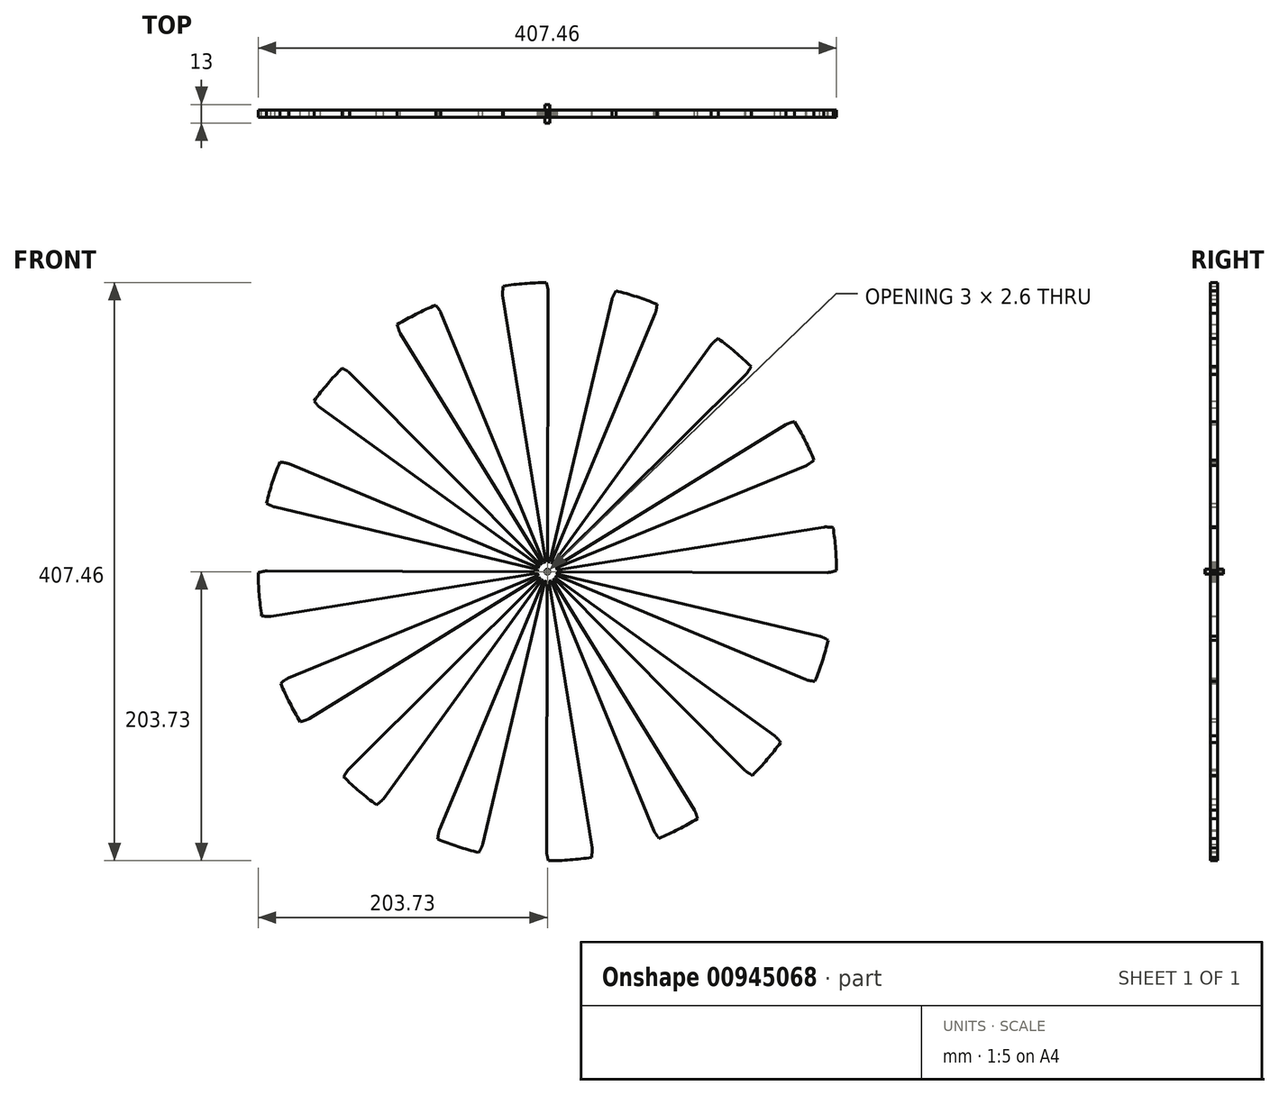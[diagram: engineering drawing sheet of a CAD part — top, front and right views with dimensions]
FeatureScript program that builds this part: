
annotation { "Feature Type Name" : "Feature", "Feature Type Description" : "" }
export const myFeature = defineFeature(function(context is Context, id is Id, definition is map)
    precondition{}
    {
        {
            assignVariable(context, id + "F0", {"name" : "Teeth", "anyValue" : 16});
        }
        {
            var Q0;
            Q0=qCreatedBy(makeId("Front.planeOp"),FACE);
            var sketch = newSketch(context, id + "F1", { "sketchPlane" : qUnion([Q0])});
            skCircle(sketch, "E0", {"center": v(0, 0) * mm, "radius": 7.73 * mm, "construction": true});
            skLineSegment(sketch, "E1", {"start": v(0, 0) * mm, "end": v(-0.42, 7.72) * mm, "construction": true});
            skLineSegment(sketch, "E2", {"start": v(0, 0) * mm, "end": v(-0.88, 7.68) * mm, "construction": true});
            skLineSegment(sketch, "E3", {"start": v(0, 0) * mm, "end": v(-1.35, 7.6) * mm, "construction": true});
            skLineSegment(sketch, "E4", {"start": v(-1.35, 7.6) * mm, "end": v(0.03, 7.85) * mm, "construction": true});
            skLineSegment(sketch, "E5", {"start": v(0, 0) * mm, "end": v(-1.8, 7.51) * mm, "construction": true});
            skLineSegment(sketch, "E6", {"start": v(-1.8, 7.51) * mm, "end": v(0.01, 7.95) * mm, "construction": true});
            skLineSegment(sketch, "E7", {"start": v(-1.35, 7.6) * mm, "end": v(-0.88, 7.68) * mm, "construction": true});
            skLineSegment(sketch, "E8", {"start": v(-1.8, 7.51) * mm, "end": v(-1.35, 7.6) * mm, "construction": true});
            skLineSegment(sketch, "E9", {"start": v(-1.35, 7.6) * mm, "end": v(-0.42, 7.72) * mm, "construction": true});
            skLineSegment(sketch, "E10", {"start": v(-1.8, 7.51) * mm, "end": v(-0.42, 7.72) * mm, "construction": true});
            skLineSegment(sketch, "E11", {"start": v(0, 0) * mm, "end": v(-3.14, 7.06) * mm, "construction": true});
            skLineSegment(sketch, "E12", {"start": v(-3.14, 7.06) * mm, "end": v(-0.16, 8.38) * mm, "construction": true});
            skLineSegment(sketch, "E13", {"start": v(0, 0) * mm, "end": v(-2.7, 7.24) * mm, "construction": true});
            skLineSegment(sketch, "E14", {"start": v(-2.7, 7.24) * mm, "end": v(-0.08, 8.22) * mm, "construction": true});
            skLineSegment(sketch, "E15", {"start": v(0, 0) * mm, "end": v(-2.26, 7.4) * mm, "construction": true});
            skLineSegment(sketch, "E16", {"start": v(-2.26, 7.4) * mm, "end": v(-0.03, 8.07) * mm, "construction": true});
            skLineSegment(sketch, "E17", {"start": v(-2.26, 7.4) * mm, "end": v(-1.8, 7.51) * mm, "construction": true});
            skLineSegment(sketch, "E18", {"start": v(-2.26, 7.4) * mm, "end": v(-2.7, 7.24) * mm, "construction": true});
            skLineSegment(sketch, "E19", {"start": v(-2.7, 7.24) * mm, "end": v(-3.14, 7.06) * mm, "construction": true});
            skLineSegment(sketch, "E20", {"start": v(-2.26, 7.4) * mm, "end": v(-0.42, 7.72) * mm, "construction": true});
            skLineSegment(sketch, "E21", {"start": v(-2.7, 7.24) * mm, "end": v(-0.42, 7.72) * mm, "construction": true});
            skLineSegment(sketch, "E22", {"start": v(-3.14, 7.06) * mm, "end": v(-0.42, 7.72) * mm, "construction": true});
            skLineSegment(sketch, "E23", {"start": v(0, 0) * mm, "end": v(-3.97, 6.63) * mm, "construction": true});
            skLineSegment(sketch, "E24", {"start": v(-3.97, 6.63) * mm, "end": v(-0.4, 8.77) * mm, "construction": true});
            skLineSegment(sketch, "E25", {"start": v(0, 0) * mm, "end": v(-4.36, 6.38) * mm, "construction": true});
            skLineSegment(sketch, "E26", {"start": v(-4.36, 6.38) * mm, "end": v(-0.55, 8.98) * mm, "construction": true});
            skLineSegment(sketch, "E27", {"start": v(0, 0) * mm, "end": v(-4.74, 6.1) * mm, "construction": true});
            skLineSegment(sketch, "E28", {"start": v(0, 0) * mm, "end": v(-3.56, 6.86) * mm, "construction": true});
            skLineSegment(sketch, "E29", {"start": v(-3.56, 6.86) * mm, "end": v(-0.26, 8.57) * mm, "construction": true});
            skLineSegment(sketch, "E30", {"start": v(-3.14, 7.06) * mm, "end": v(-3.56, 6.86) * mm, "construction": true});
            skLineSegment(sketch, "E31", {"start": v(-3.56, 6.86) * mm, "end": v(-3.97, 6.63) * mm, "construction": true});
            skLineSegment(sketch, "E32", {"start": v(-3.97, 6.63) * mm, "end": v(-4.36, 6.38) * mm, "construction": true});
            skLineSegment(sketch, "E33", {"start": v(-4.36, 6.38) * mm, "end": v(-4.74, 6.1) * mm, "construction": true});
            skLineSegment(sketch, "E34", {"start": v(-0.42, 7.72) * mm, "end": v(-3.56, 6.86) * mm, "construction": true});
            skLineSegment(sketch, "E35", {"start": v(-0.42, 7.72) * mm, "end": v(-3.97, 6.63) * mm, "construction": true});
            skLineSegment(sketch, "E36", {"start": v(-0.42, 7.72) * mm, "end": v(-4.36, 6.38) * mm, "construction": true});
            skLineSegment(sketch, "E37", {"start": v(-0.42, 7.72) * mm, "end": v(-4.74, 6.1) * mm, "construction": true});
            skCircle(sketch, "E38", {"center": v(0, 0) * mm, "radius": 8 * mm, "construction": true});
            skCircle(sketch, "E39", {"center": v(0, 0) * mm, "radius": 9 * mm});
            skPoint(sketch, "E40", {"position": v(0, 8) * mm});
            skLineSegment(sketch, "E41", {"start": v(0, 0) * mm, "end": v(-0.84, 8.56) * mm, "construction": true});
            skPoint(sketch, "E42.MirrorP", {"position": v(-1.56, 7.85) * mm});
            skLineSegment(sketch, "E43", {"start": v(-1.56, 7.85) * mm, "end": v(0, 0) * mm, "construction": true});
            skLineSegment(sketch, "E44", {"start": v(0, 0) * mm, "end": v(0, 8) * mm, "construction": true});
            skLineSegment(sketch, "E45", {"start": v(-0.88, 7.68) * mm, "end": v(-0.42, 7.72) * mm, "construction": true});
            skLineSegment(sketch, "E46", {"start": v(0.03, 7.85) * mm, "end": v(0.01, 7.95) * mm, "construction": true});
            skLineSegment(sketch, "E47", {"start": v(0, 0) * mm, "end": v(0, 10.19) * mm, "construction": true});
            skCircle(sketch, "E48", {"center": v(0, 0) * mm, "radius": 7 * mm});
            skSolve(sketch);
        }
        {
            var Q0;
            Q0=qCreatedBy(makeId("Front.planeOp"),FACE);
            var sketch = newSketch(context, id + "F2", { "sketchPlane" : qUnion([Q0])});
            skCircle(sketch, "E49.0", {"center": v(0, 0) * mm, "radius": 8 * mm, "construction": true});
            skPoint(sketch, "E50.0", {"position": v(-0.55, 8.98) * mm});
            skPoint(sketch, "E50.1", {"position": v(-0.4, 8.77) * mm});
            skPoint(sketch, "E50.2", {"position": v(-0.26, 8.57) * mm});
            skPoint(sketch, "E50.3", {"position": v(-0.16, 8.38) * mm});
            skPoint(sketch, "E50.4", {"position": v(-0.08, 8.22) * mm});
            skPoint(sketch, "E50.6", {"position": v(0.01, 7.95) * mm});
            skPoint(sketch, "E50.7", {"position": v(0.03, 7.85) * mm});
            skPoint(sketch, "E50.8", {"position": v(-0.03, 8.07) * mm});
            skLineSegment(sketch, "E51.0", {"start": v(0, 0) * mm, "end": v(-0.84, 8.56) * mm, "construction": true});
            skFitSpline(sketch, "E52", {"points": [v(-0.77, 203.73) * mm, v(-0.39, 202.42) * mm, v(-0.08, 201.25) * mm, v(0.16, 200.2) * mm, v(0.34, 199.29) * mm, v(0.47, 198.5) * mm, v(0.56, 197.87) * mm, v(0.6, 197.37) * mm], "startDerivative": vector(6.57, -22.38) * mm, "endDerivative": vector(1.47, -14.1) * mm});
            skFitSpline(sketch, "E53.MirrorCS", {"points": [v(-31.11, 201.34) * mm, v(-31.28, 200) * mm, v(-31.4, 198.78) * mm, v(-31.48, 197.7) * mm, v(-31.51, 196.78) * mm, v(-31.52, 196) * mm, v(-31.5, 195.35) * mm, v(-31.48, 194.85) * mm], "startDerivative": vector(-2.99, -23.13) * mm, "endDerivative": vector(0.76, -14.15) * mm});
            skCircle(sketch, "E54", {"center": v(0, 0) * mm, "radius": 0.05 * mm});
            skCircle(sketch, "E55.0", {"center": v(0, 0) * mm, "radius": 7 * mm});
            skArc(sketch, "E56", {"start": v(-0.77, 203.73) * mm, "mid": v(-15.98, 203.1) * mm, "end": v(-31.11, 201.34) * mm});
            skLineSegment(sketch, "E57", {"start": v(-31.48, 194.85) * mm, "end": v(0, 0) * mm});
            skLineSegment(sketch, "E58", {"start": v(0, 0) * mm, "end": v(0.6, 197.37) * mm});
            skSolve(sketch);
        }
        {
            var Q0;
            {var subQ1=sQuery(id+"F2.wireOp",EDGE,"E52");var subQ9=sQuery(id+"F2.wireOp",EDGE,"rA0usyOi-Jm6w-jZNR-JSDv-ujEcH4bsm2Ol");var subQ11=makeQuery(id+"F2.imprint","INTERSECT",VERTEX,{"derivedFrom":[subQ1,subQ9]});Q0=makeQuery(id+"F2.imprint","IMPRINT",FACE,{"disambiguationData":[TD([[makeQuery(id+"F2.imprint","IMPRINT",EDGE,{"disambiguationData":[TD([[subQ11,1.0]])],"derivedFrom":subQ1}),-1.0]])]});}
            var Q1;
            {var subQ0=sQuery(id+"F2.wireOp",EDGE,"QqPcIgQ4-TZE6-73E5-WQaq-ugCT5JtziKyn");var subQ1=sQuery(id+"F2.wireOp",EDGE,"90be38e0-c88f-493d-85a8-1201295b9109.0");var subQ2=makeQuery(id+"F2.imprint","INTERSECT",VERTEX,{"derivedFrom":[subQ1,subQ0]});Q1=makeQuery(id+"F2.imprint","IMPRINT",FACE,{"disambiguationData":[TD([[makeQuery(id+"F2.imprint","IMPRINT",EDGE,{"disambiguationData":[TD([[subQ2,1.0]])],"derivedFrom":subQ1}),1.0]])]});}
            var Q2;
            {var subQ0=sQuery(id+"F2.wireOp",EDGE,"QqPcIgQ4-TZE6-73E5-WQaq-ugCT5JtziKyn");var subQ1=sQuery(id+"F2.wireOp",EDGE,"90be38e0-c88f-493d-85a8-1201295b9109.0");var subQ2=makeQuery(id+"F2.imprint","INTERSECT",VERTEX,{"derivedFrom":[subQ1,subQ0]});Q2=makeQuery(id+"F2.imprint","IMPRINT",FACE,{"disambiguationData":[TD([[makeQuery(id+"F2.imprint","IMPRINT",EDGE,{"disambiguationData":[TD([[subQ2,-1.0]])],"derivedFrom":subQ1}),1.0]])]});}
            var Q3;
            {var subQ1=sQuery(id+"F2.wireOp",EDGE,"E52");var subQ8=sQuery(id+"F2.wireOp",EDGE,"b861a5ab-cd51-40f1-92ab-cea0f5fe0d4d.1");var subQ11=makeQuery(id+"F2.imprint","INTERSECT",VERTEX,{"derivedFrom":[subQ1,subQ8]});Q3=makeQuery(id+"F2.imprint","IMPRINT",FACE,{"disambiguationData":[TD([[makeQuery(id+"F2.imprint","IMPRINT",EDGE,{"disambiguationData":[TD([[subQ11,1.0]])],"derivedFrom":subQ1}),-1.0]])]});}
            var Q4;
            {var subQ0=sQuery(id+"F2.wireOp",EDGE,"b861a5ab-cd51-40f1-92ab-cea0f5fe0d4d.0");var subQ1=sQuery(id+"F2.wireOp",EDGE,"E54");var subQ2=makeQuery(id+"F2.imprint","INTERSECT",VERTEX,{"derivedFrom":[subQ1,subQ0]});Q4=makeQuery(id+"F2.imprint","IMPRINT",FACE,{"disambiguationData":[TD([[makeQuery(id+"F2.imprint","IMPRINT",EDGE,{"disambiguationData":[TD([[subQ2,-1.0]])],"derivedFrom":subQ1}),-1.0]])]});}
            var Q5;
            {var subQ0=sQuery(id+"F2.wireOp",EDGE,"b861a5ab-cd51-40f1-92ab-cea0f5fe0d4d.0");var subQ1=sQuery(id+"F2.wireOp",EDGE,"E54");var subQ2=makeQuery(id+"F2.imprint","INTERSECT",VERTEX,{"derivedFrom":[subQ1,subQ0]});Q5=makeQuery(id+"F2.imprint","IMPRINT",FACE,{"disambiguationData":[TD([[makeQuery(id+"F2.imprint","IMPRINT",EDGE,{"disambiguationData":[TD([[subQ2,1.0]])],"derivedFrom":subQ1}),-1.0]])]});}
            extrude(context, id + "F3", {"entities" : qUnion([Q0, Q1, Q2, Q3, Q4, Q5]), "offsetDistance" : 25 * mm, "depth" : 5 * mm, "symmetric" : true});
        }
        {
            var Q0;
            Q0=makeQuery(id+"FdV6txGXfAbNHnU_2.opFillet","BLEND_FACE",FACE,{"disambiguationData":[OSD([sQuery(id+"F2.wireOp",EDGE,"E55.0"),sQuery(id+"F2.wireOp",EDGE,"E57")])]});
            var Q1;
            Q1=makeQuery(id+"F3.opExtrude","SWEPT_FACE",FACE,{"disambiguationData":[OSD([sQuery(id+"F2.wireOp",EDGE,"E57")])]});
            var Q2;
            Q2=makeQuery(id+"F3.opExtrude","SWEPT_FACE",FACE,{"disambiguationData":[OSD([sQuery(id+"F2.wireOp",EDGE,"E53.MirrorCS")])]});
            var Q3;
            Q3=makeQuery(id+"F3.opExtrude","SWEPT_FACE",FACE,{"disambiguationData":[OSD([sQuery(id+"F2.wireOp",EDGE,"E56")])]});
            var Q4;
            Q4=makeQuery(id+"F3.opExtrude","SWEPT_FACE",FACE,{"disambiguationData":[OSD([sQuery(id+"F2.wireOp",EDGE,"E52")])]});
            var Q5;
            Q5=makeQuery(id+"F3.opExtrude","SWEPT_FACE",FACE,{"disambiguationData":[OSD([sQuery(id+"F2.wireOp",EDGE,"E58")])]});
            var Q6;
            Q6=makeQuery(id+"FdV6txGXfAbNHnU_2.opFillet","BLEND_FACE",FACE,{"disambiguationData":[OSD([sQuery(id+"F2.wireOp",EDGE,"E55.0"),sQuery(id+"F2.wireOp",EDGE,"E58")])]});
            var Q7;
            Q7=makeQuery(id+"F3.opExtrude","SWEPT_FACE",FACE,{"disambiguationData":[OSD([sQuery(id+"F2.wireOp",EDGE,"E55.0")])]});
            circularPattern(context, id + "F4", {"faces" : qUnion([Q0, Q1, Q2, Q3, Q4, Q5, Q6]), "axis" : qUnion([Q7]), "angle" : 360 * degree, "instanceCount" : round(getVariable(context, 'Teeth')), "equalSpace" : true, "patternType" : PatternType.FACE});
        }
        {
            var Q0;
            Q0=qCreatedBy(makeId("Front.planeOp"),FACE);
            var sketch = newSketch(context, id + "F5", { "sketchPlane" : qUnion([Q0])});
            skCircle(sketch, "E59", {"center": v(0, 0) * mm, "radius": 6.5 * mm});
            skSolve(sketch);
        }
        {
            var Q0;
            Q0=makeQuery(id+"F5.imprint","IMPRINT",FACE,{"disambiguationData":[TD([[makeQuery(id+"F5.imprint","IMPRINT",EDGE,{"derivedFrom":sQuery(id+"F5.wireOp",EDGE,"E59")}),1.0]])]});
            extrude(context, id + "F6", {"entities" : qUnion([Q0]), "operationType" : NewBodyOperationType.ADD, "depth" : 2 * mm, "offsetDistance" : 25 * mm, "symmetric" : true});
        }
        {
            var Q0;
            Q0=qCreatedBy(makeId("Front.planeOp"),FACE);
            var sketch = newSketch(context, id + "F7", { "sketchPlane" : qUnion([Q0])});
            skArc(sketch, "E60", {"start": v(-0.5, 2.96) * mm, "mid": v(-1.83, 2.38) * mm, "end": v(-2.73, 1.25) * mm});
            skLineSegment(sketch, "E61", {"start": v(-2.73, 1.25) * mm, "end": v(-5.36, 1.25) * mm});
            skLineSegment(sketch, "E62", {"start": v(-0.5, 2.96) * mm, "end": v(-0.5, 5.48) * mm});
            skLineSegment(sketch, "E63.MirrorCS", {"start": v(-2.73, -1.25) * mm, "end": v(-5.36, -1.25) * mm});
            skLineSegment(sketch, "E64.MirrorCS", {"start": v(0.5, 2.96) * mm, "end": v(0.5, 5.48) * mm});
            skLineSegment(sketch, "E65.MirrorCS", {"start": v(2.73, 1.25) * mm, "end": v(5.36, 1.25) * mm});
            skLineSegment(sketch, "E66.MirrorCS", {"start": v(2.73, -1.25) * mm, "end": v(5.36, -1.25) * mm});
            skLineSegment(sketch, "E67.MirrorCS", {"start": v(-0.5, -2.96) * mm, "end": v(-0.5, -5.48) * mm});
            skLineSegment(sketch, "E68.MirrorCS", {"start": v(0.5, -2.96) * mm, "end": v(0.5, -5.48) * mm});
            skArc(sketch, "E69.trimOffspring", {"start": v(-2.73, -1.25) * mm, "mid": v(-1.83, -2.38) * mm, "end": v(-0.5, -2.96) * mm});
            skArc(sketch, "E70.trimOffspring", {"start": v(0.5, -2.96) * mm, "mid": v(1.83, -2.38) * mm, "end": v(2.73, -1.25) * mm});
            skArc(sketch, "E71.trimOffspring", {"start": v(2.73, 1.25) * mm, "mid": v(1.83, 2.38) * mm, "end": v(0.5, 2.96) * mm});
            skArc(sketch, "E72", {"start": v(0.5, 5.48) * mm, "mid": v(0, 5.5) * mm, "end": v(-0.5, 5.48) * mm});
            skArc(sketch, "E73.trimOffspring", {"start": v(5.36, -1.25) * mm, "mid": v(5.5, 0) * mm, "end": v(5.36, 1.25) * mm});
            skArc(sketch, "E74.trimOffspring", {"start": v(-0.5, -5.48) * mm, "mid": v(0, -5.5) * mm, "end": v(0.5, -5.48) * mm});
            skArc(sketch, "E75.trimOffspring", {"start": v(-5.36, 1.25) * mm, "mid": v(-5.5, 0) * mm, "end": v(-5.36, -1.25) * mm});
            skSolve(sketch);
        }
        {
            var Q0;
            Q0 = qSketchRegion(id + "F7", true);
            extrude(context, id + "F8", {"entities" : qUnion([Q0]), "operationType" : NewBodyOperationType.ADD, "depth" : 4 * mm, "offsetDistance" : 25 * mm, "symmetric" : true});
        }
        {
            var Q0;
            Q0=qCreatedBy(makeId("Front.planeOp"),FACE);
            var sketch = newSketch(context, id + "F9", { "sketchPlane" : qUnion([Q0])});
            skCircle(sketch, "E76", {"center": v(0, 0) * mm, "radius": 1.75 * mm});
            skSolve(sketch);
        }
        {
            var Q0;
            Q0 = qSketchRegion(id + "F9", true);
            extrude(context, id + "F10", {"entities" : qUnion([Q0]), "operationType" : NewBodyOperationType.ADD, "depth" : 13 * mm, "offsetDistance" : 25 * mm, "symmetric" : true});
        }
        {
            var Q0;
            Q0=makeQuery(id+"F10.opExtrude","CAP_FACE",FACE,{"disambiguationData":[OSD([sQuery(id+"F9.wireOp",EDGE,"E76")])],"isStart":false});
            var sketch = newSketch(context, id + "F11", { "sketchPlane" : qUnion([Q0])});
            skCircle(sketch, "E77.cCircle", {"center": v(0, 0) * mm, "radius": 1.5 * mm, "construction": true});
            skLineSegment(sketch, "E77.0", {"start": v(1.5, 0) * mm, "end": v(0.75, -1.3) * mm});
            skLineSegment(sketch, "E77.1", {"start": v(0.75, -1.3) * mm, "end": v(-0.75, -1.3) * mm});
            skLineSegment(sketch, "E77.2", {"start": v(-0.75, -1.3) * mm, "end": v(-1.5, 0) * mm});
            skLineSegment(sketch, "E77.3", {"start": v(-1.5, 0) * mm, "end": v(-0.75, 1.3) * mm});
            skLineSegment(sketch, "E77.4", {"start": v(-0.75, 1.3) * mm, "end": v(0.75, 1.3) * mm});
            skLineSegment(sketch, "E77.5", {"start": v(0.75, 1.3) * mm, "end": v(1.5, 0) * mm});
            skSolve(sketch);
        }
        {
            var Q0;
            Q0 = qSketchRegion(id + "F11", true);
            extrude(context, id + "F12", {"entities" : qUnion([Q0]), "operationType" : NewBodyOperationType.REMOVE, "endBound" : BoundingType.THROUGH_ALL, "oppositeDirection" : true, "depth" : 25 * mm, "offsetDistance" : 25 * mm});
        }
    });
